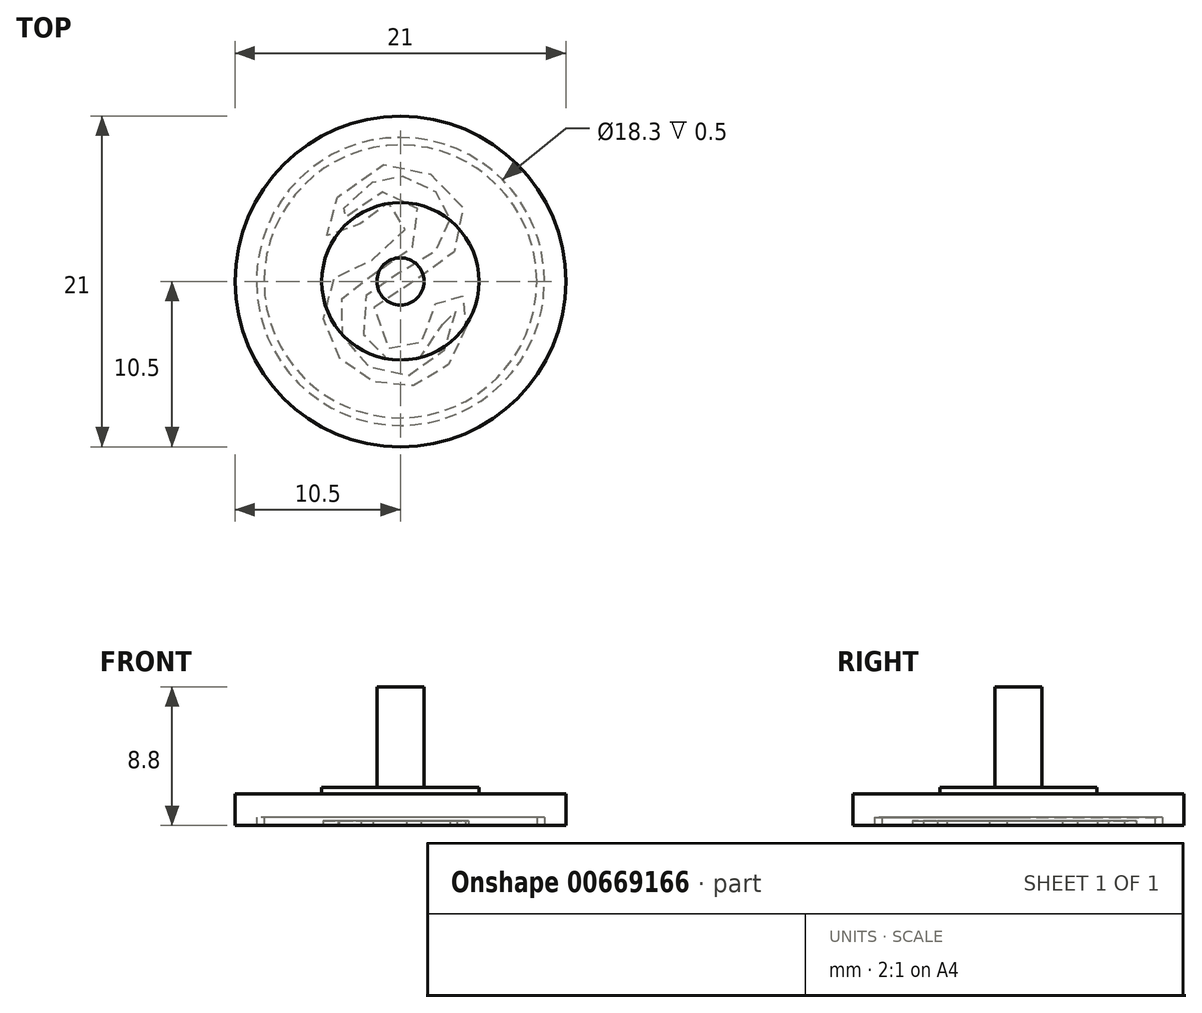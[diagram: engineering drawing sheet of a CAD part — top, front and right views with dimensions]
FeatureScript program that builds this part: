
annotation { "Feature Type Name" : "Feature", "Feature Type Description" : "" }
export const myFeature = defineFeature(function(context is Context, id is Id, definition is map)
    precondition{}
    {
        {
            var Q0;
            Q0=qCreatedBy(makeId("Top.planeOp"),FACE);
            var sketch = newSketch(context, id + "F0", { "sketchPlane" : qUnion([Q0])});
            skCircle(sketch, "E0", {"center": v(0, 0) * mm, "radius": 10.5 * mm});
            skCircle(sketch, "E1", {"center": v(0, 0) * mm, "radius": 5 * mm});
            skCircle(sketch, "E2", {"center": v(0, 0) * mm, "radius": 1.5 * mm});
            skSolve(sketch);
        }
        {
            var Q0;
            Q0=makeQuery(id+"F0.imprint","IMPRINT",FACE,{"disambiguationData":[TD([[makeQuery(id+"F0.imprint","IMPRINT",EDGE,{"derivedFrom":sQuery(id+"F0.wireOp",EDGE,"E0")}),1.0]])]});
            extrude(context, id + "F1", {"entities" : qUnion([Q0]), "depth" : 2 * mm, "offsetDistance" : 25.4 * mm});
        }
        {
            var Q0;
            Q0=makeQuery(id+"F0.imprint","IMPRINT",FACE,{"disambiguationData":[TD([[makeQuery(id+"F0.imprint","IMPRINT",EDGE,{"derivedFrom":sQuery(id+"F0.wireOp",EDGE,"E1")}),1.0]])]});
            extrude(context, id + "F2", {"entities" : qUnion([Q0]), "operationType" : NewBodyOperationType.ADD, "depth" : 2.4 * mm, "offsetDistance" : 25.4 * mm});
        }
        {
            var Q0;
            Q0=makeQuery(id+"F0.imprint","IMPRINT",FACE,{"disambiguationData":[TD([[makeQuery(id+"F0.imprint","IMPRINT",EDGE,{"derivedFrom":sQuery(id+"F0.wireOp",EDGE,"E2")}),1.0]])]});
            extrude(context, id + "F3", {"entities" : qUnion([Q0]), "operationType" : NewBodyOperationType.ADD, "depth" : 8.8 * mm, "offsetDistance" : 25.4 * mm});
        }
        {
            var Q0;
            Q0=qCreatedBy(makeId("Top.planeOp"),FACE);
            var sketch = newSketch(context, id + "F4", { "sketchPlane" : qUnion([Q0])});
            skCircle(sketch, "E3", {"center": v(0, 0) * mm, "radius": 9.15 * mm});
            skCircle(sketch, "E4", {"center": v(0, 0) * mm, "radius": 8.66 * mm});
            skFitSpline(sketch, "E5", {"points": [v(4.17, -2.9) * mm, v(2.73, -5.63) * mm, v(0, -6.72) * mm, v(-2.8, -5.8) * mm, v(-4.67, -3.42) * mm, v(-4.4, 0) * mm, v(-1.58, 1.48) * mm, v(0.38, 3.88) * mm, v(-1.14, 5) * mm, v(-3.2, 3.08) * mm, v(-4.86, 3.15) * mm, v(-2.3, 6.94) * mm, v(1.79, 6.89) * mm, v(4.13, 4) * mm, v(1.76, 0.38) * mm, v(-1.67, -1.6) * mm, v(-0.38, -4.46) * mm, v(1.57, -3.51) * mm, v(2.54, -0.99) * mm, v(4.05, -1.01) * mm, v(4.17, -2.9) * mm]});
            skFitSpline(sketch, "E6", {"points": [v(2.68, -2.73) * mm, v(2.97, -1.98) * mm, v(3.52, -1.95) * mm, v(2.47, -4.8) * mm, v(0, -6.04) * mm, v(-2.5, -5.06) * mm, v(-3.89, -2.8) * mm, v(-3.48, -0.73) * mm, v(-0.72, 1.01) * mm, v(1.25, 3.1) * mm, v(0.44, 5.4) * mm, v(-2.43, 5.14) * mm, v(-3.85, 3.73) * mm, v(-3.65, 4.56) * mm, v(-1.88, 6.24) * mm, v(-0.43, 6.73) * mm, v(1.49, 6.24) * mm, v(2.94, 4.82) * mm, v(3.06, 3.4) * mm, v(1.6, 1.36) * mm, v(-1.18, 0) * mm, v(-2.4, -1.46) * mm, v(-2.06, -4.01) * mm, v(-0.49, -5.06) * mm, v(1.25, -4.82) * mm, v(2.68, -2.73) * mm]});
            skSolve(sketch);
        }
        {
            var Q0;
            Q0=makeQuery(id+"F4.imprint","IMPRINT",FACE,{"disambiguationData":[TD([[makeQuery(id+"F4.imprint","IMPRINT",EDGE,{"derivedFrom":sQuery(id+"F4.wireOp",EDGE,"E3")}),1.0]])]});
            extrude(context, id + "F5", {"entities" : qUnion([Q0]), "operationType" : NewBodyOperationType.REMOVE, "depth" : .5 * mm, "offsetDistance" : 25.4 * mm});
        }
        {
            var Q0;
            Q0=makeQuery(id+"F4.imprint","IMPRINT",FACE,{"disambiguationData":[TD([[makeQuery(id+"F4.imprint","IMPRINT",EDGE,{"derivedFrom":sQuery(id+"F4.wireOp",EDGE,"E5")}),-1.0]])]});
            extrude(context, id + "F6", {"entities" : qUnion([Q0]), "operationType" : NewBodyOperationType.REMOVE, "depth" : 0.3 * mm, "offsetDistance" : 25.4 * mm});
        }
        {
            var Q0;
            Q0=makeQuery(id+"F4.imprint","IMPRINT",FACE,{"disambiguationData":[TD([[makeQuery(id+"F4.imprint","IMPRINT",EDGE,{"derivedFrom":sQuery(id+"F4.wireOp",EDGE,"E6")}),-1.0]])]});
            extrude(context, id + "F7", {"entities" : qUnion([Q0]), "operationType" : NewBodyOperationType.ADD, "depth" : 0.4 * mm, "offsetDistance" : 25.4 * mm});
        }
    });
